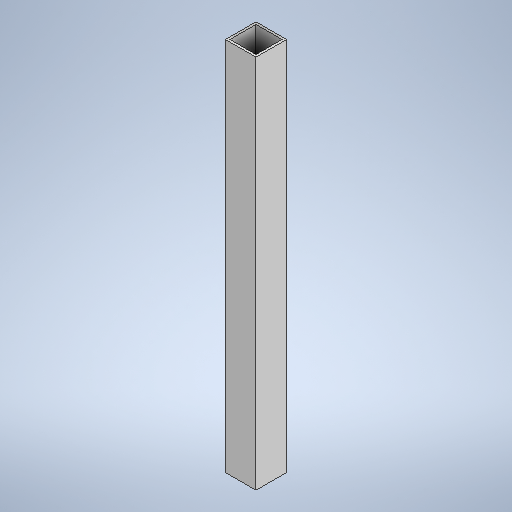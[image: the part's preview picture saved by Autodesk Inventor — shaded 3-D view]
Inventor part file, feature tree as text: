
AUTODESK INVENTOR PART (.ipt)
format: ipt  version: 2025 (Build 290162000, 162)  size: 254,464 bytes
history: native  units: in
note: dims shown in document units (in); Inventor stores cm internally (conversion verified against a paired STEP export)
features: extrude x1, sketch x1
ambient origin geometry x8: Origin, YZ Plane, XZ Plane, XY Plane, X Axis, Y Axis, Z Axis, Center Point
bodies: Solid1 (feature_tree)
feature tree (2):
  extrude  "Extrusion1"  Depth=1.5748in
  sketch  "Sketch1"  dims[d0=1.5748in d1=1.5748in d2=1.3386in d3=1.3386in d4=0.1181in d5=19.2913in d6=0.0in]
